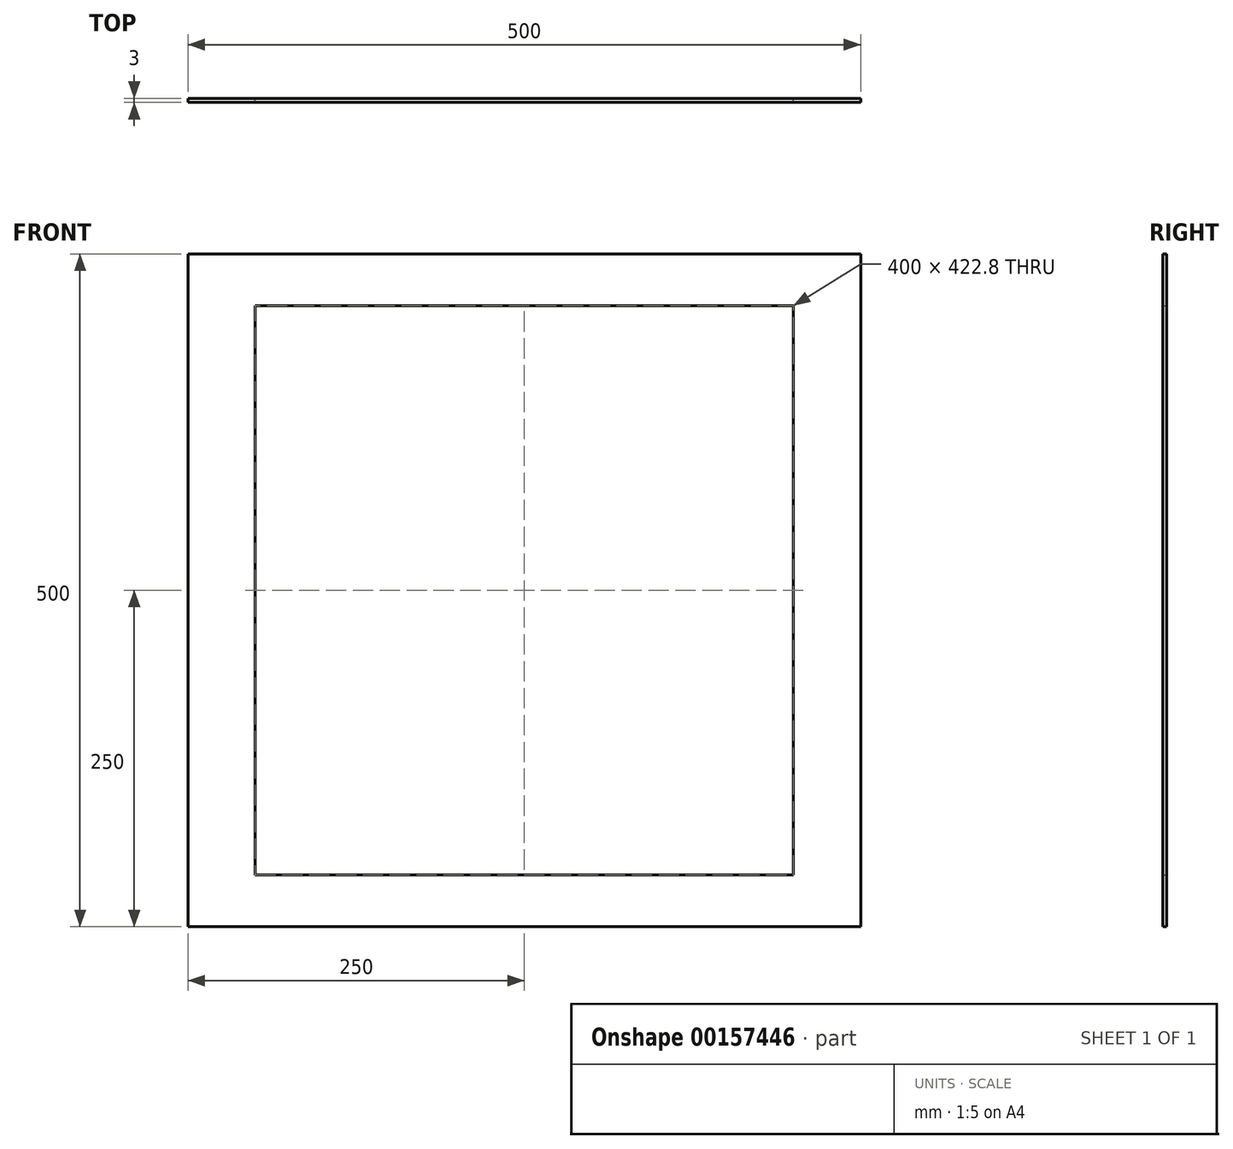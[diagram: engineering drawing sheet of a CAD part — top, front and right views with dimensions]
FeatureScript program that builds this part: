
annotation { "Feature Type Name" : "Feature", "Feature Type Description" : "" }
export const myFeature = defineFeature(function(context is Context, id is Id, definition is map)
    precondition{}
    {
        {
            var Q0;
            Q0=qCreatedBy(makeId("Front.planeOp"),FACE);
            var sketch = newSketch(context, id + "F0", { "sketchPlane" : qUnion([Q0])});
            skLineSegment(sketch, "E0.bottom", {"start": v(250, 250) * mm, "end": v(-250, 250) * mm});
            skLineSegment(sketch, "E0.top", {"start": v(250, -250) * mm, "end": v(-250, -250) * mm});
            skLineSegment(sketch, "E0.left", {"start": v(250, 250) * mm, "end": v(250, -250) * mm});
            skLineSegment(sketch, "E0.right", {"start": v(-250, 250) * mm, "end": v(-250, -250) * mm});
            skPoint(sketch, "E0.middle", {"position": v(0, 0) * mm});
            skLineSegment(sketch, "E1.bottom", {"start": v(-200, 211.4) * mm, "end": v(200, 211.4) * mm});
            skLineSegment(sketch, "E1.top", {"start": v(-200, -211.4) * mm, "end": v(200, -211.4) * mm});
            skLineSegment(sketch, "E1.left", {"start": v(-200, 211.4) * mm, "end": v(-200, -211.4) * mm});
            skLineSegment(sketch, "E1.right", {"start": v(200, 211.4) * mm, "end": v(200, -211.4) * mm});
            skSolve(sketch);
        }
        {
            var Q0;
            Q0 = qSketchRegion(id + "F0", true);
            extrude(context, id + "F1", {"entities" : qUnion([Q0]), "depth" : 3 * mm});
        }
    });
